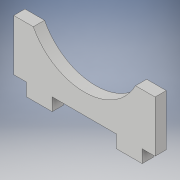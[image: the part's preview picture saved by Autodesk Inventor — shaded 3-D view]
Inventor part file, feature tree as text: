
AUTODESK INVENTOR PART (.ipt)
format: ipt  version: 2018 (Build 220112000, 112)  size: 108,032 bytes
history: native  units: in
note: dims shown in document units (in); Inventor stores cm internally (conversion verified against a paired STEP export)
features: extrude x1, sketch x1
ambient origin geometry x8: Origin, YZ Plane, XZ Plane, XY Plane, X Axis, Y Axis, Z Axis, Center Point
bodies: Solid1 (feature_tree)
feature tree (2):
  extrude  "Extrusion1"  Depth=0.25in
  sketch  "Sketch1"  dims[d1=1.0in d6=0.25in d7=0.5in d8=0.25in d9=0.25in d10=0.5in d11=0.2188in d12=0.0in]
